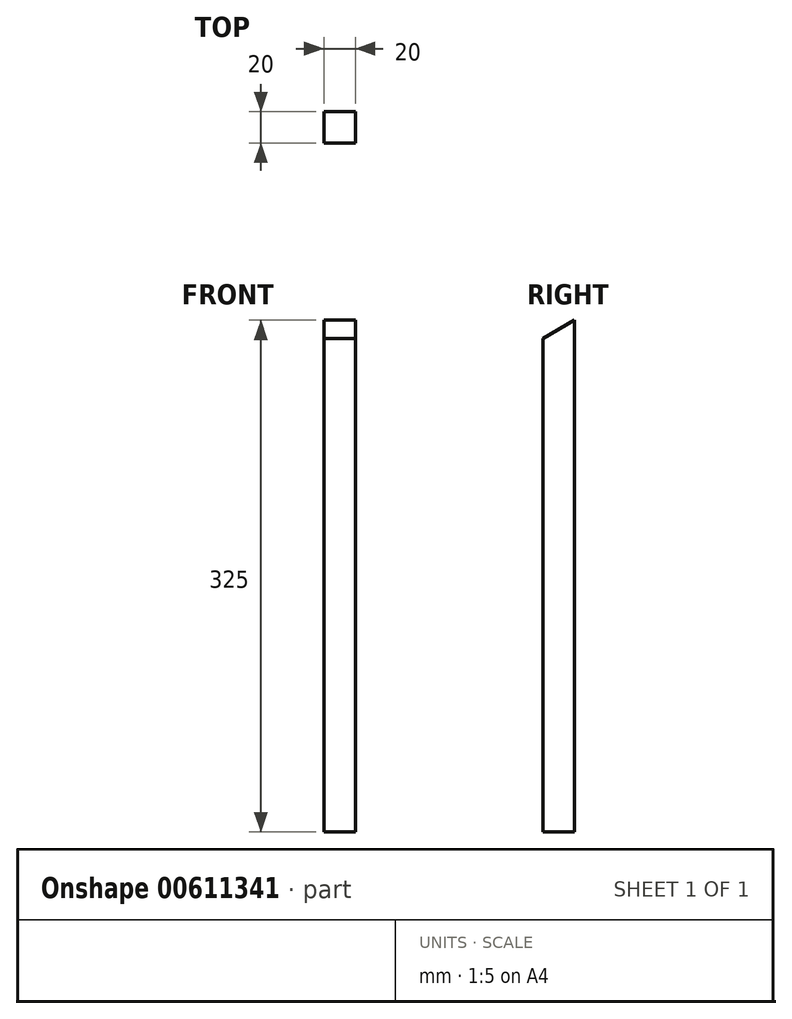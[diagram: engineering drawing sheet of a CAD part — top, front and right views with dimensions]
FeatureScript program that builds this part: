
annotation { "Feature Type Name" : "Feature", "Feature Type Description" : "" }
export const myFeature = defineFeature(function(context is Context, id is Id, definition is map)
    precondition{}
    {
        {
            var Q0;
            Q0=qCreatedBy(makeId("Front.planeOp"),FACE);
            var sketch = newSketch(context, id + "F0", { "sketchPlane" : qUnion([Q0])});
            skLineSegment(sketch, "E0.bottom", {"start": v(-10, 162.5) * mm, "end": v(10, 162.5) * mm});
            skLineSegment(sketch, "E0.top", {"start": v(-10, -162.5) * mm, "end": v(10, -162.5) * mm});
            skLineSegment(sketch, "E0.left", {"start": v(-10, 162.5) * mm, "end": v(-10, -162.5) * mm});
            skLineSegment(sketch, "E0.right", {"start": v(10, 162.5) * mm, "end": v(10, -162.5) * mm});
            skPoint(sketch, "E0.middle", {"position": v(0, 0) * mm});
            skSolve(sketch);
        }
        {
            var Q0;
            Q0=makeQuery(id+"F0.imprint","IMPRINT",FACE,{"disambiguationData":[TD([[makeQuery(id+"F0.imprint","IMPRINT",EDGE,{"derivedFrom":sQuery(id+"F0.wireOp",EDGE,"E0.bottom")}),-1.0]])]});
            extrude(context, id + "F1", {"entities" : qUnion([Q0]), "depth" : 20 * mm, "offsetDistance" : 25 * mm});
        }
        {
            var Q0;
            Q0=makeQuery(id+"F1.opExtrude","SWEPT_FACE",FACE,{"disambiguationData":[OSD([sQuery(id+"F0.wireOp",EDGE,"E0.left")])]});
            var sketch = newSketch(context, id + "F2", { "sketchPlane" : qUnion([Q0])});
            skLineSegment(sketch, "E1", {"start": v(0, 162.5) * mm, "end": v(20, 150.95) * mm});
            skLineSegment(sketch, "E2", {"start": v(20, 150.95) * mm, "end": v(20, 150.95) * mm});
            skLineSegment(sketch, "E3", {"start": v(20, 162.5) * mm, "end": v(20, 162.5) * mm});
            skLineSegment(sketch, "E4", {"start": v(20, 162.5) * mm, "end": v(0, 162.5) * mm});
            skSolve(sketch);
        }
        {
            var Q0;
            Q0 = qSketchRegion(id + "F2", true);
            var Q1;
            {var subQ0=sQuery(id+"F2.wireOp",EDGE,"E1");Q1=makeQuery(id+"F2.imprint","IMPRINT",FACE,{"disambiguationData":[TD([[makeQuery(id+"F2.imprint","IMPRINT",EDGE,{"derivedFrom":subQ0}),1.0]])]});}
            extrude(context, id + "F3", {"entities" : qUnion([Q0, Q1]), "operationType" : NewBodyOperationType.REMOVE, "endBound" : BoundingType.THROUGH_ALL, "oppositeDirection" : true, "depth" : 25 * mm, "offsetDistance" : 25 * mm});
        }
    });
